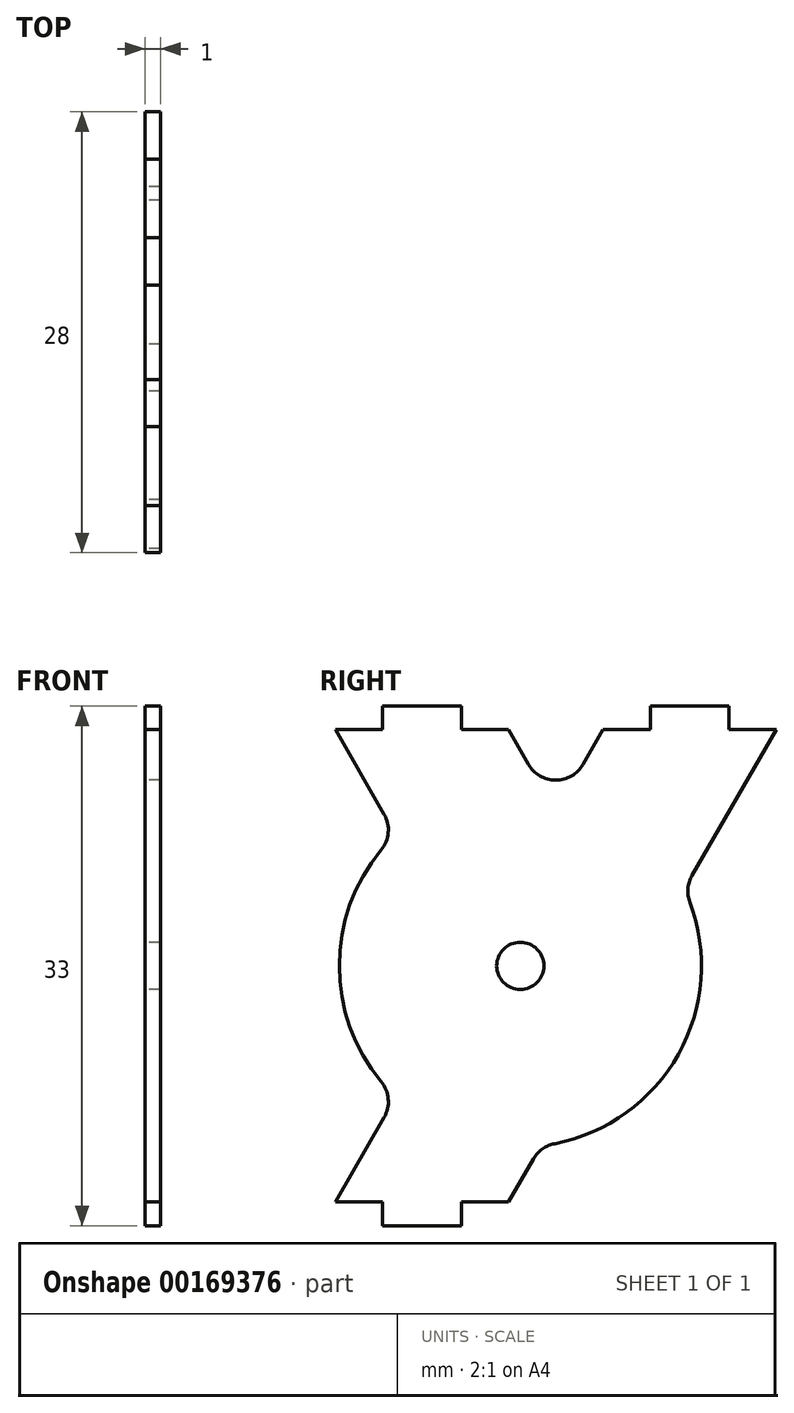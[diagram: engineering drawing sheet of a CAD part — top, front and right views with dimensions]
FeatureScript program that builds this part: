
annotation { "Feature Type Name" : "Feature", "Feature Type Description" : "" }
export const myFeature = defineFeature(function(context is Context, id is Id, definition is map)
    precondition{}
    {
        {
            var Q0;
            Q0=qCreatedBy(makeId("Right.planeOp"),FACE);
            var sketch = newSketch(context, id + "F0", { "sketchPlane" : qUnion([Q0])});
            skLineSegment(sketch, "E0.bottom", {"start": v(-15.25, 15) * mm, "end": v(-12.25, 15) * mm});
            skLineSegment(sketch, "E0.top", {"start": v(-15.25, -15) * mm, "end": v(-12.25, -15) * mm});
            skLineSegment(sketch, "E1.top", {"start": v(-12.25, -16.5) * mm, "end": v(-7.25, -16.5) * mm});
            skLineSegment(sketch, "E1.left", {"start": v(-12.25, -15) * mm, "end": v(-12.25, -16.5) * mm});
            skLineSegment(sketch, "E1.right", {"start": v(-7.25, -15) * mm, "end": v(-7.25, -16.5) * mm});
            skLineSegment(sketch, "E2.top", {"start": v(-12.25, 16.5) * mm, "end": v(-7.25, 16.5) * mm});
            skLineSegment(sketch, "E2.left", {"start": v(-12.25, 15) * mm, "end": v(-12.25, 16.5) * mm});
            skLineSegment(sketch, "E2.right", {"start": v(-7.25, 15) * mm, "end": v(-7.25, 16.5) * mm});
            skLineSegment(sketch, "E3.top", {"start": v(4.75, 16.5) * mm, "end": v(9.75, 16.5) * mm});
            skLineSegment(sketch, "E3.left", {"start": v(4.75, 15) * mm, "end": v(4.75, 16.5) * mm});
            skLineSegment(sketch, "E3.right", {"start": v(9.75, 15) * mm, "end": v(9.75, 16.5) * mm});
            skLineSegment(sketch, "E4.trimOffspring", {"start": v(-7.25, 15) * mm, "end": v(-4.25, 15) * mm});
            skLineSegment(sketch, "E5.trimOffspring", {"start": v(9.75, 15) * mm, "end": v(12.75, 15) * mm});
            skLineSegment(sketch, "E6.trimOffspring", {"start": v(-7.25, -15) * mm, "end": v(-4.25, -15) * mm});
            skCircle(sketch, "E7", {"center": v(-3.5, 0) * mm, "radius": 1.5 * mm});
            skArc(sketch, "E8", {"start": v(-2.19, -11.42) * mm, "mid": v(6.54, -5.6) * mm, "end": v(6.91, 4.89) * mm});
            skLineSegment(sketch, "E9", {"start": v(-15.25, -15) * mm, "end": v(-11.4, -8.35) * mm});
            skLineSegment(sketch, "E10", {"start": v(-4.25, -15) * mm, "end": v(-2.19, -11.42) * mm});
            skLineSegment(sketch, "E11", {"start": v(-15.25, 15) * mm, "end": v(-11.4, 8.35) * mm});
            skLineSegment(sketch, "E12", {"start": v(-4.25, 15) * mm, "end": v(-2.98, 12.8) * mm});
            skArc(sketch, "E13.trimOffspring", {"start": v(-11.4, 8.35) * mm, "mid": v(-15, 0) * mm, "end": v(-11.4, -8.35) * mm});
            skLineSegment(sketch, "E14", {"start": v(12.75, 15) * mm, "end": v(6.91, 4.89) * mm});
            skLineSegment(sketch, "E15", {"start": v(1.75, 15) * mm, "end": v(0.48, 12.8) * mm});
            skLineSegment(sketch, "E16.trimOffspring", {"start": v(1.75, 15) * mm, "end": v(4.75, 15) * mm});
            skArc(sketch, "E17", {"start": v(-2.98, 12.8) * mm, "mid": v(-1.25, 11.8) * mm, "end": v(0.48, 12.8) * mm});
            skSolve(sketch);
        }
        {
            var Q0;
            Q0 = qSketchRegion(id + "F0", true);
            extrude(context, id + "F1", {"entities" : qUnion([Q0]), "depth" : 1 * mm});
        }
        {
            var Q0;
            Q0=makeQuery(id+"F1.opExtrude","SWEPT_EDGE",EDGE,{"disambiguationData":[OSD([sQuery(id+"F0.wireOp",EDGE,"E11"),sQuery(id+"F0.wireOp",EDGE,"E13.trimOffspring")])]});
            var Q1;
            Q1=makeQuery(id+"F1.opExtrude","SWEPT_EDGE",EDGE,{"disambiguationData":[OSD([sQuery(id+"F0.wireOp",EDGE,"E9"),sQuery(id+"F0.wireOp",EDGE,"E13.trimOffspring")])]});
            var Q2;
            Q2=makeQuery(id+"F1.opExtrude","SWEPT_EDGE",EDGE,{"disambiguationData":[OSD([sQuery(id+"F0.wireOp",EDGE,"E8"),sQuery(id+"F0.wireOp",EDGE,"E10")])]});
            var Q3;
            Q3=makeQuery(id+"F1.opExtrude","SWEPT_EDGE",EDGE,{"disambiguationData":[OSD([sQuery(id+"F0.wireOp",EDGE,"E8"),sQuery(id+"F0.wireOp",EDGE,"E14")])]});
            fillet(context, id + "F2", {"entities" : qUnion([Q0, Q1, Q2, Q3]), "radius" : 2 * mm, "tangentPropagation" : true, "allowEdgeOverflow" : false});
        }
    });
